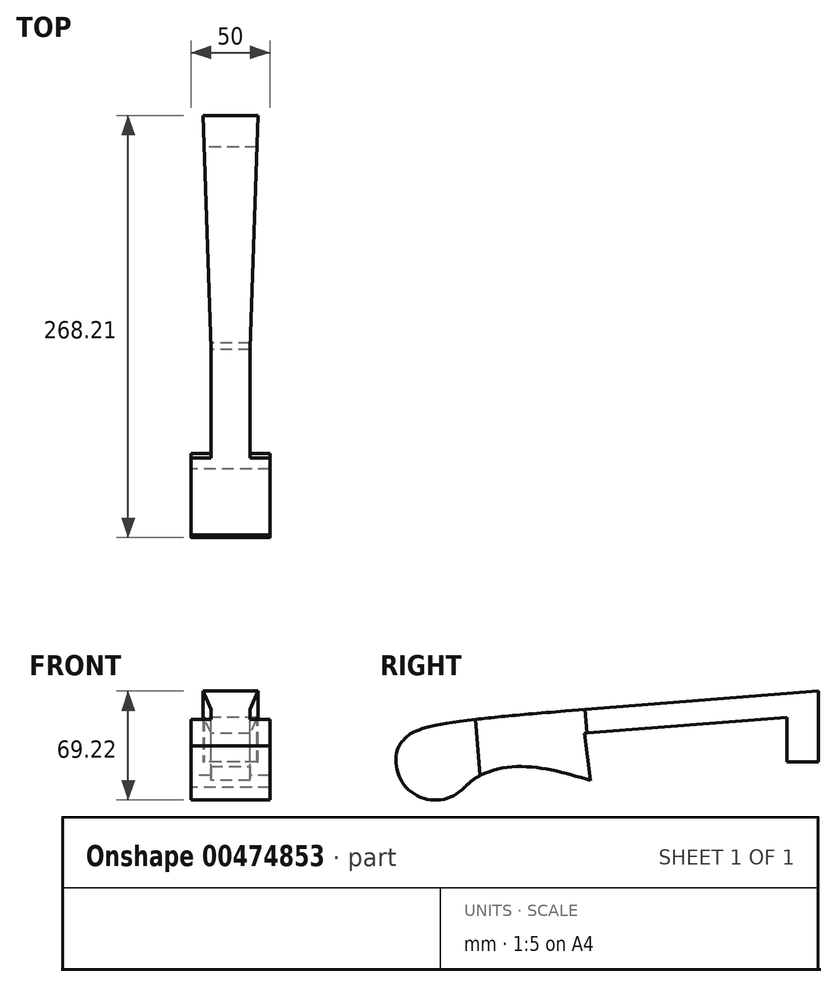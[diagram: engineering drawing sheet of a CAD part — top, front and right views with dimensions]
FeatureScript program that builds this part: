
annotation { "Feature Type Name" : "Feature", "Feature Type Description" : "" }
export const myFeature = defineFeature(function(context is Context, id is Id, definition is map)
    precondition{}
    {
        {
            var Q0;
            Q0=qCreatedBy(makeId("Right.planeOp"),FACE);
            var sketch = newSketch(context, id + "F0", { "sketchPlane" : qUnion([Q0])});
            skLineSegment(sketch, "E0", {"start": v(-10, 0) * mm, "end": v(10, 0) * mm});
            skLineSegment(sketch, "E1", {"start": v(10, 0) * mm, "end": v(10, 45) * mm});
            skLineSegment(sketch, "E2", {"start": v(10, 45) * mm, "end": v(-150.5, 32.37) * mm});
            skLineSegment(sketch, "E3", {"start": v(-10, 0) * mm, "end": v(-10, 28.38) * mm});
            skLineSegment(sketch, "E4", {"start": v(-10, 28.38) * mm, "end": v(-138.6, 18.26) * mm});
            skLineSegment(sketch, "E5", {"start": v(-150.5, 32.37) * mm, "end": v(-261.16, 23.66) * mm, "construction": true});
            skLineSegment(sketch, "E6", {"start": v(-138.6, 18.26) * mm, "end": v(-134.6, -11.74) * mm});
            skLineSegment(sketch, "E7", {"start": v(-134.6, -11.74) * mm, "end": v(-255.1, -26.34) * mm, "construction": true});
            skLineSegment(sketch, "E8", {"start": v(-255.1, -26.34) * mm, "end": v(-261.16, 23.66) * mm, "construction": true});
            skArc(sketch, "E9", {"start": v(-256.38, 10.17) * mm, "mid": v(-246.54, -20.36) * mm, "end": v(-214.75, -16.08) * mm});
            skFitSpline(sketch, "E10", {"points": [v(-150.5, 32.37) * mm, v(-256.38, 10.17) * mm], "startDerivative": vector(-303.43, -23.88) * mm, "endDerivative": vector(-24.34, -29.66) * mm});
            skFitSpline(sketch, "E11", {"points": [v(-214.75, -16.08) * mm, v(-134.6, -11.74) * mm], "startDerivative": vector(63.62, 62.88) * mm, "endDerivative": vector(80.1, -24.83) * mm});
            skSolve(sketch);
        }
        {
            var Q0;
            Q0=makeQuery(id+"F0.imprint","IMPRINT",FACE,{"disambiguationData":[TD([[makeQuery(id+"F0.imprint","IMPRINT",EDGE,{"derivedFrom":sQuery(id+"F0.wireOp",EDGE,"E0")}),1.0]])]});
            extrude(context, id + "F1", {"entities" : qUnion([Q0]), "endBound" : BoundingType.SYMMETRIC, "depth" : 50 * mm});
        }
        {
            var Q0;
            Q0=makeQuery(id+"F1.opExtrude","SWEPT_FACE",FACE,{"disambiguationData":[OSD([sQuery(id+"F0.wireOp",EDGE,"E2")])]});
            var sketch = newSketch(context, id + "F2", { "sketchPlane" : qUnion([Q0])});
            skLineSegment(sketch, "E12", {"start": v(-12.5, -135.11) * mm, "end": v(12.5, -135.11) * mm, "construction": true});
            skLineSegment(sketch, "E13", {"start": v(12.5, -135.11) * mm, "end": v(17.5, 13.5) * mm});
            skLineSegment(sketch, "E14", {"start": v(17.5, 13.5) * mm, "end": v(-17.5, 13.5) * mm, "construction": true});
            skLineSegment(sketch, "E15", {"start": v(-17.5, 13.5) * mm, "end": v(-12.5, -135.11) * mm});
            skLineSegment(sketch, "E16", {"start": v(0, 13.5) * mm, "end": v(0, -254.69) * mm, "construction": true});
            skLineSegment(sketch, "E17", {"start": v(40.13, -134.18) * mm, "end": v(123.04, -131.4) * mm});
            skLineSegment(sketch, "E18", {"start": v(123.04, -131.4) * mm, "end": v(123.04, 13.5) * mm});
            skLineSegment(sketch, "E19", {"start": v(123.04, 13.5) * mm, "end": v(17.5, 13.5) * mm});
            skLineSegment(sketch, "E20", {"start": v(-49.57, 11.58) * mm, "end": v(-65.63, -135.11) * mm});
            skLineSegment(sketch, "E21", {"start": v(12.5, -135.11) * mm, "end": v(12.5, -204.79) * mm});
            skLineSegment(sketch, "E22", {"start": v(12.5, -204.79) * mm, "end": v(40.13, -204.79) * mm});
            skLineSegment(sketch, "E23", {"start": v(40.13, -204.79) * mm, "end": v(40.13, -134.18) * mm});
            skLineSegment(sketch, "E24", {"start": v(-12.5, -135.11) * mm, "end": v(-12.5, -204.79) * mm});
            skLineSegment(sketch, "E25", {"start": v(-12.5, -204.79) * mm, "end": v(-43.54, -204.79) * mm});
            skLineSegment(sketch, "E26", {"start": v(-43.54, -204.79) * mm, "end": v(-65.63, -135.11) * mm});
            skLineSegment(sketch, "E27", {"start": v(-17.5, 13.5) * mm, "end": v(-43.3, 13.5) * mm});
            skLineSegment(sketch, "E28", {"start": v(-43.3, 13.5) * mm, "end": v(-49.57, 11.58) * mm});
            skSolve(sketch);
        }
        {
            var Q0;
            Q0 = qSketchRegion(id + "F2", true);
            extrude(context, id + "F3", {"entities" : qUnion([Q0]), "operationType" : NewBodyOperationType.REMOVE, "oppositeDirection" : true, "depth" : 50 * mm});
        }
    });
